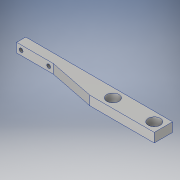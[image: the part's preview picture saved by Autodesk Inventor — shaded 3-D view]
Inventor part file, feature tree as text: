
AUTODESK INVENTOR PART (.ipt)
format: ipt  version: 2017 (Build 210142000, 142)  size: 136,704 bytes
history: native  units: in
note: dims shown in document units (in); Inventor stores cm internally (conversion verified against a paired STEP export)
features: sketch x3, hole x2, projected_geometry x2, extrude x1
ambient origin geometry x8: Origin, YZ Plane, XZ Plane, XY Plane, X Axis, Y Axis, Z Axis, Center Point
bodies: Solid1 (feature_tree)
feature tree (8):
  sketch  "Sketch1"  dims[d5=1.75in d6=0.5in]
  extrude  "Extrusion2"  Depth=0.5in
  hole  "Hole4"  [1 undecoded]
  hole  "Hole5"  [1 undecoded]
  sketch  "Sketch5"  dims[d7=1.75in d10=1.75in]
  projected_geometry  "Projected Loop4"
  sketch  "Sketch6"  dims[d16=0.25in d55=0.25in d56=0.25in d57=0.0in d58=1.25in d59=4.0in d60=0.25in d61=0.25in d62=0.25in d63=1.125in d64=0.5in d65=0.33in d66=0.75in d67=0.375in d68=0.25in d69=0.5635in d70=1.0in d71=0.8108in d72=0.25in d73=0.125in d74=0.125in d75=0.75in d76=0.125in d77=0.104in d78=0.276in d79=0.375in d80=0.25in d81=0.5635in d82=0.432in d83=0.8108in]
  projected_geometry  "Projected Loop5"
note: 2 required parameter values undecoded (feature->parameter linkage not recoverable at this tier; creation-order binding heuristic only, values carry confidence <= 0.55)
